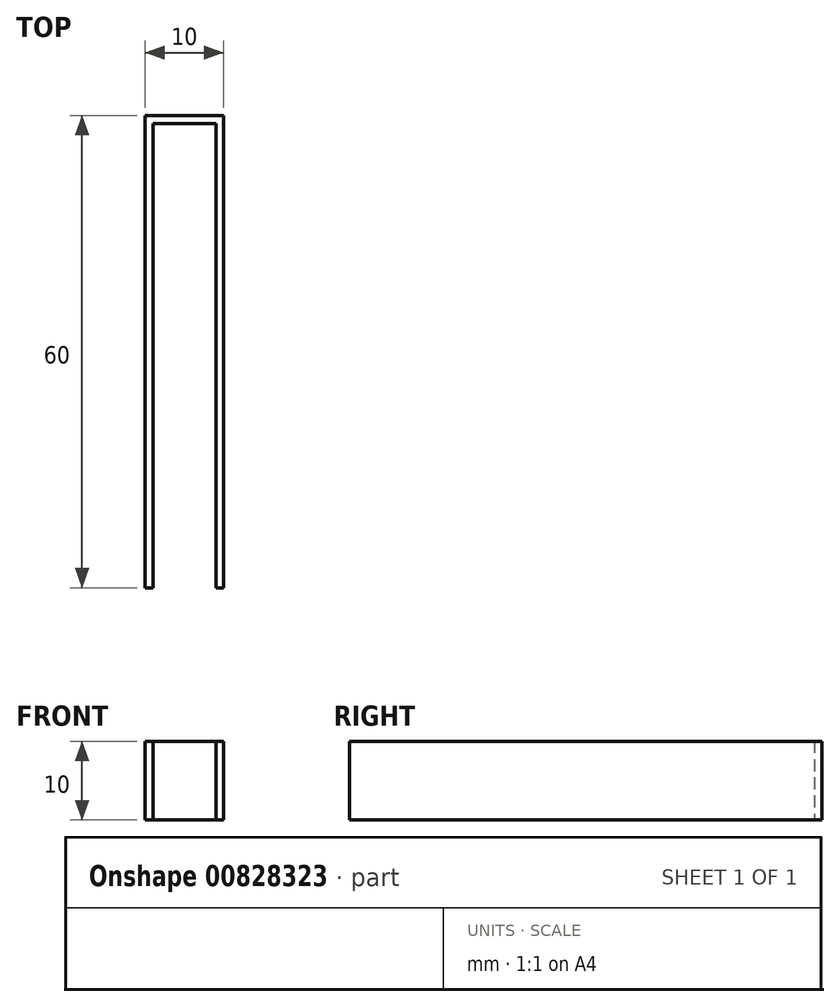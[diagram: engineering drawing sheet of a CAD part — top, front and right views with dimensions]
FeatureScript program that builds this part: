
annotation { "Feature Type Name" : "Feature", "Feature Type Description" : "" }
export const myFeature = defineFeature(function(context is Context, id is Id, definition is map)
    precondition{}
    {
        {
            var Q0;
            Q0=qCreatedBy(makeId("Top.planeOp"),FACE);
            var sketch = newSketch(context, id + "F0", { "sketchPlane" : qUnion([Q0])});
            skLineSegment(sketch, "E0", {"start": v(-7.5, 70) * mm, "end": v(2.5, 70) * mm});
            skLineSegment(sketch, "E1", {"start": v(2.5, 70) * mm, "end": v(2.5, 10) * mm});
            skLineSegment(sketch, "E2", {"start": v(2.5, 10) * mm, "end": v(-7.5, 10) * mm});
            skLineSegment(sketch, "E3", {"start": v(-7.5, 10) * mm, "end": v(-7.5, 70) * mm});
            skLineSegment(sketch, "E4", {"start": v(-6.5, 69) * mm, "end": v(1.5, 69) * mm});
            skLineSegment(sketch, "E5", {"start": v(1.5, 69) * mm, "end": v(1.5, 10) * mm});
            skLineSegment(sketch, "E6", {"start": v(1.5, 10) * mm, "end": v(-6.5, 10) * mm});
            skLineSegment(sketch, "E7", {"start": v(-6.5, 10) * mm, "end": v(-6.5, 69) * mm});
            skLineSegment(sketch, "E8", {"start": v(-55.92, 0) * mm, "end": v(45.13, 0) * mm});
            skSolve(sketch);
        }
        {
            var Q0;
            Q0=makeQuery(id+"F0.imprint","IMPRINT",FACE,{"disambiguationData":[TD([[makeQuery(id+"F0.imprint","IMPRINT",EDGE,{"derivedFrom":sQuery(id+"F0.wireOp",EDGE,"E0")}),-1.0]])]});
            extrude(context, id + "F1", {"entities" : qUnion([Q0]), "depth" : 10 * mm, "offsetDistance" : 25 * mm});
        }
    });
